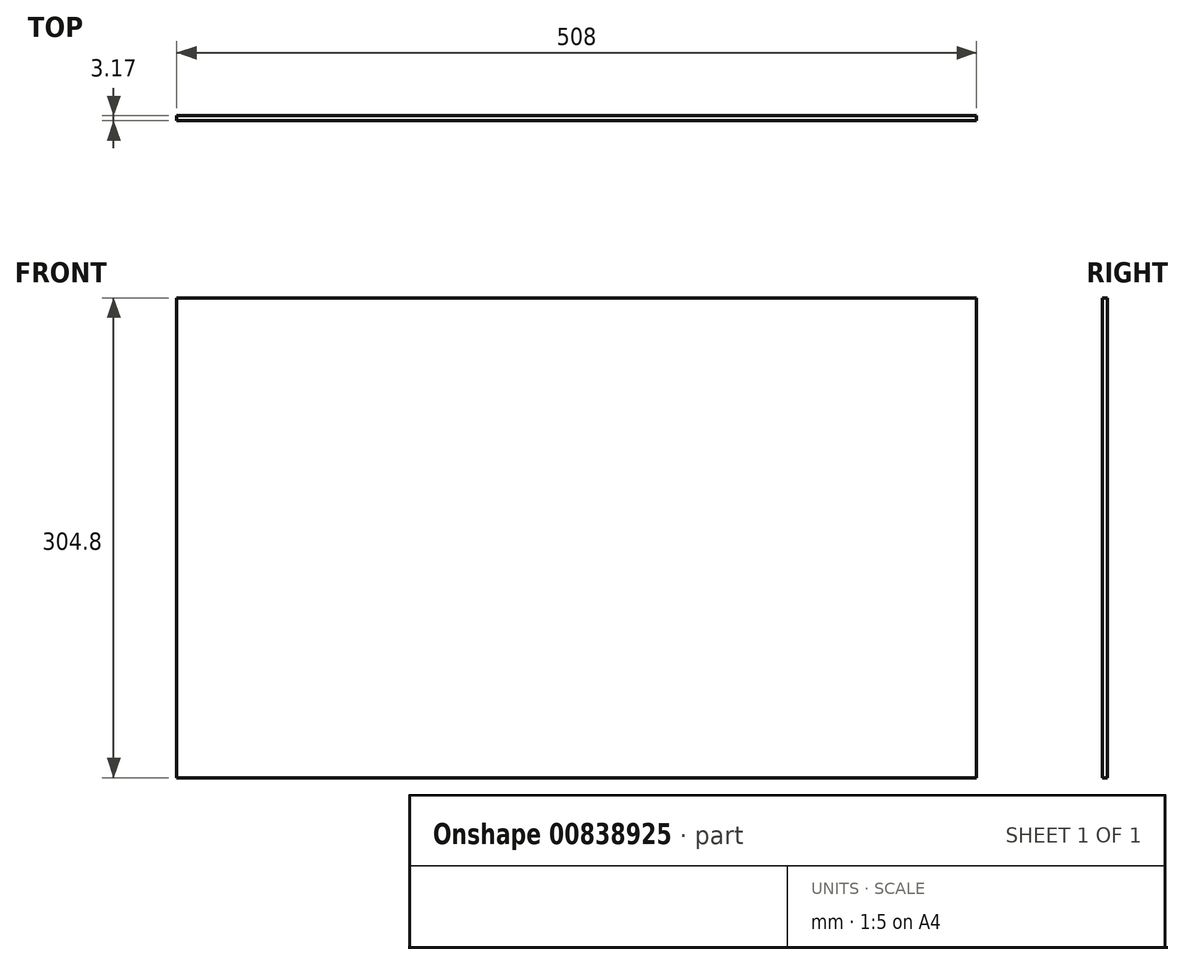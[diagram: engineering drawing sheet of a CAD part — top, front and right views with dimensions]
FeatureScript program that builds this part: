
annotation { "Feature Type Name" : "Feature", "Feature Type Description" : "" }
export const myFeature = defineFeature(function(context is Context, id is Id, definition is map)
    precondition{}
    {
        {
            var Q0;
            Q0=qCreatedBy(makeId("Front.planeOp"),FACE);
            var sketch = newSketch(context, id + "F0", { "sketchPlane" : qUnion([Q0])});
            skLineSegment(sketch, "E0", {"start": v(0, 0) * mm, "end": v(0, 304.8) * mm});
            skLineSegment(sketch, "E1", {"start": v(0, 304.8) * mm, "end": v(508, 304.8) * mm});
            skLineSegment(sketch, "E2", {"start": v(508, 304.8) * mm, "end": v(508, 0) * mm});
            skLineSegment(sketch, "E3", {"start": v(508, 0) * mm, "end": v(0, 0) * mm});
            skSolve(sketch);
        }
        {
            var Q0;
            Q0 = qSketchRegion(id + "F0", true);
            extrude(context, id + "F1", {"entities" : qUnion([Q0]), "depth" : 3.17 * mm, "offsetDistance" : 25.4 * mm});
        }
    });
